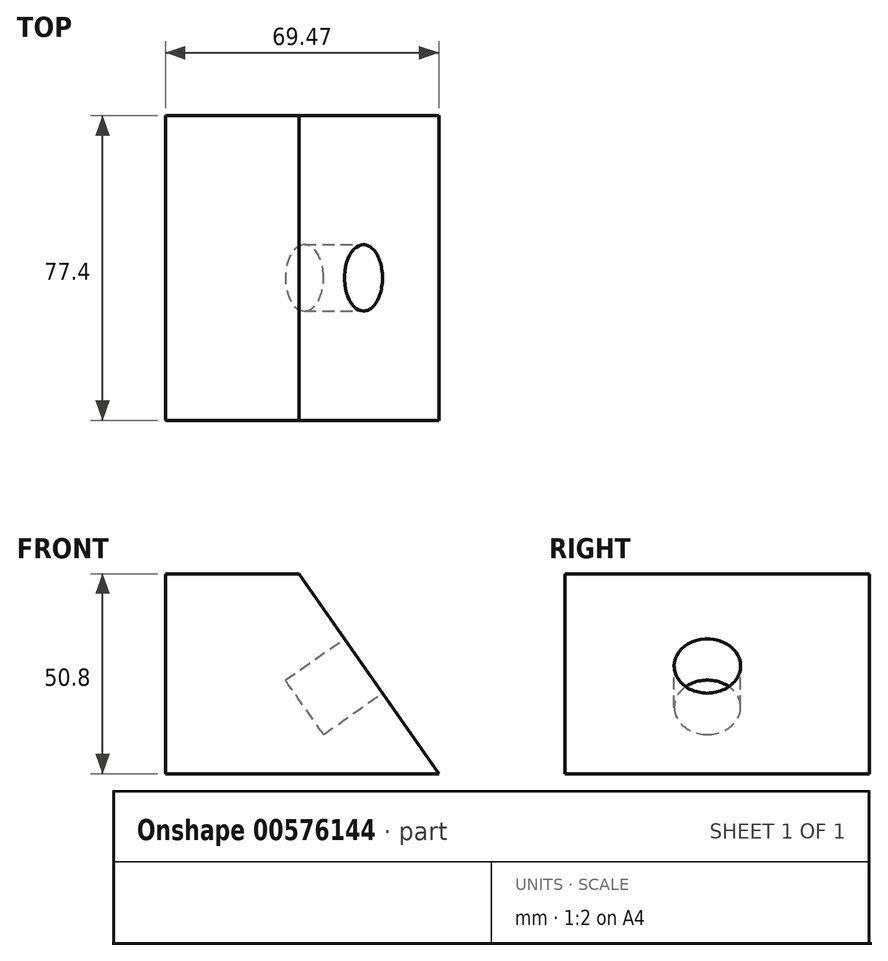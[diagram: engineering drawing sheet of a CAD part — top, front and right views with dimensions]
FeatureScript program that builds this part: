
annotation { "Feature Type Name" : "Feature", "Feature Type Description" : "" }
export const myFeature = defineFeature(function(context is Context, id is Id, definition is map)
    precondition{}
    {
        {
            var Q0;
            Q0=qCreatedBy(makeId("Top.planeOp"),FACE);
            var sketch = newSketch(context, id + "F0", { "sketchPlane" : qUnion([Q0])});
            skLineSegment(sketch, "E0.bottom", {"start": v(0, 41.2) * mm, "end": v(-33.9, 41.2) * mm});
            skLineSegment(sketch, "E0.top", {"start": v(0, -36.2) * mm, "end": v(-33.9, -36.2) * mm});
            skLineSegment(sketch, "E0.left", {"start": v(0, 41.2) * mm, "end": v(0, -36.2) * mm});
            skLineSegment(sketch, "E0.right", {"start": v(-33.9, 41.2) * mm, "end": v(-33.9, -36.2) * mm});
            skLineSegment(sketch, "E1.bottom", {"start": v(0, 41.2) * mm, "end": v(50.6, 41.2) * mm});
            skLineSegment(sketch, "E1.top", {"start": v(0, -36.2) * mm, "end": v(50.6, -36.2) * mm});
            skLineSegment(sketch, "E1.right", {"start": v(50.6, 41.2) * mm, "end": v(50.6, -36.2) * mm});
            skSolve(sketch);
        }
        {
            var Q0;
            Q0=makeQuery(id+"F0.imprint","IMPRINT",FACE,{"disambiguationData":[TD([[makeQuery(id+"F0.imprint","IMPRINT",EDGE,{"derivedFrom":sQuery(id+"F0.wireOp",EDGE,"E0.bottom")}),1.0]])]});
            extrude(context, id + "F1", {"entities" : qUnion([Q0]), "depth" : 50.8 * mm, "offsetDistance" : 25.4 * mm});
        }
        {
            var Q0;
            Q0=makeQuery(id+"F1.opExtrude","CAP_EDGE",EDGE,{"disambiguationData":[OSD([sQuery(id+"F0.wireOp",EDGE,"E0.left")])],"isStart":false});
            cPlane(context, id + "F2", {"entities" : qUnion([Q0]), "cplaneType" : CPlaneType.LINE_ANGLE, "offset" : 25.4 * mm, "angle" : 125 * degree, "width" : 152.4 * mm, "height" : 152.4 * mm});
        }
        {
            var Q0;
            Q0=makeQuery(id+"F0.imprint","IMPRINT",FACE,{"disambiguationData":[TD([[makeQuery(id+"F0.imprint","IMPRINT",EDGE,{"derivedFrom":sQuery(id+"F0.wireOp",EDGE,"E1.bottom")}),-1.0]])]});
            var Q1;
            Q1=qCreatedBy(id+"F2.planeOp",FACE);
            extrude(context, id + "F3", {"entities" : qUnion([Q0]), "operationType" : NewBodyOperationType.ADD, "endBound" : BoundingType.UP_TO_SURFACE, "depth" : 25.4 * mm, "endBoundEntityFace" : qUnion([Q1]), "offsetDistance" : 25.4 * mm});
        }
        {
            var Q0;
            Q0=qCreatedBy(makeId("Top.planeOp"),FACE);
            var sketch = newSketch(context, id + "F4", { "sketchPlane" : qUnion([Q0])});
            skLineSegment(sketch, "E2.bottom", {"start": v(-33.9, 41.2) * mm, "end": v(0, 41.2) * mm});
            skLineSegment(sketch, "E2.top", {"start": v(-33.9, 37.5) * mm, "end": v(0, 37.5) * mm});
            skLineSegment(sketch, "E2.left", {"start": v(-33.9, 41.2) * mm, "end": v(-33.9, 37.5) * mm});
            skLineSegment(sketch, "E2.right", {"start": v(0, 41.2) * mm, "end": v(0, 37.5) * mm});
            skLineSegment(sketch, "E3.bottom", {"start": v(0, 41.2) * mm, "end": v(35.57, 41.2) * mm});
            skLineSegment(sketch, "E3.top", {"start": v(0, 37.5) * mm, "end": v(35.57, 37.5) * mm});
            skLineSegment(sketch, "E3.right", {"start": v(35.57, 41.2) * mm, "end": v(35.57, 37.5) * mm});
            skSolve(sketch);
        }
        {
            var Q0;
            Q0=sQuery(id+"F4.wireOp",EDGE,"E2.top");
            var Q1;
            Q1=sQuery(id+"F4.wireOp",EDGE,"E2.bottom");
            var Q2;
            Q2=sQuery(id+"F4.wireOp",EDGE,"E2.left");
            var Q3;
            Q3=sQuery(id+"F4.wireOp",EDGE,"E2.right");
            extrude(context, id + "F5", {"bodyType" : ToolBodyType.SURFACE, "surfaceEntities" : qUnion([Q0, Q1, Q2, Q3]), "depth" : 57.15 * mm, "offsetDistance" : 25.4 * mm});
        }
        {
            var Q0;
            Q0=makeQuery(id+"F5.opExtrude","CAP_EDGE",EDGE,{"disambiguationData":[OSD([sQuery(id+"F4.wireOp",EDGE,"E2.right")])],"isStart":false});
            cPlane(context, id + "F6", {"entities" : qUnion([Q0]), "cplaneType" : CPlaneType.LINE_ANGLE, "offset" : 25.4 * mm, "angle" : 125 * degree, "width" : 152.4 * mm, "height" : 152.4 * mm});
        }
        {
            var Q0;
            Q0=sQuery(id+"F4.wireOp",EDGE,"E2.right");
            var Q1;
            Q1=sQuery(id+"F4.wireOp",EDGE,"E3.bottom");
            var Q2;
            Q2=sQuery(id+"F4.wireOp",EDGE,"E3.top");
            var Q3;
            Q3=sQuery(id+"F4.wireOp",EDGE,"E3.right");
            var Q4;
            Q4=qCreatedBy(id+"F6.planeOp",FACE);
            extrude(context, id + "F7", {"bodyType" : ToolBodyType.SURFACE, "surfaceEntities" : qUnion([Q0, Q1, Q2, Q3]), "endBound" : BoundingType.UP_TO_SURFACE, "depth" : 25.4 * mm, "endBoundEntityFace" : qUnion([Q4]), "offsetDistance" : 25.4 * mm});
        }
        {
            var Q0;
            Q0=makeQuery(id+"F3.opExtrude","CAP_FACE",FACE,{"disambiguationData":[OSD([sQuery(id+"F0.wireOp",EDGE,"E1.bottom"),sQuery(id+"F0.wireOp",EDGE,"E1.top"),sQuery(id+"F0.wireOp",EDGE,"E0.left"),sQuery(id+"F0.wireOp",EDGE,"E1.right")])],"isStart":false});
            var sketch = newSketch(context, id + "F8", { "sketchPlane" : qUnion([Q0])});
            skCircle(sketch, "E4", {"center": v(0, 13.03) * mm, "radius": 8.43 * mm});
            skSolve(sketch);
        }
        {
            var Q0;
            Q0 = qSketchRegion(id + "F8", true);
            var Q1;
            Q1=qCreatedBy(makeId("Top.planeOp"),FACE);
            extrude(context, id + "F9", {"entities" : qUnion([Q0]), "operationType" : NewBodyOperationType.REMOVE, "oppositeDirection" : true, "depth" : 18.29 * mm, "endBoundEntityFace" : qUnion([Q1]), "offsetDistance" : 25.4 * mm});
        }
    });
